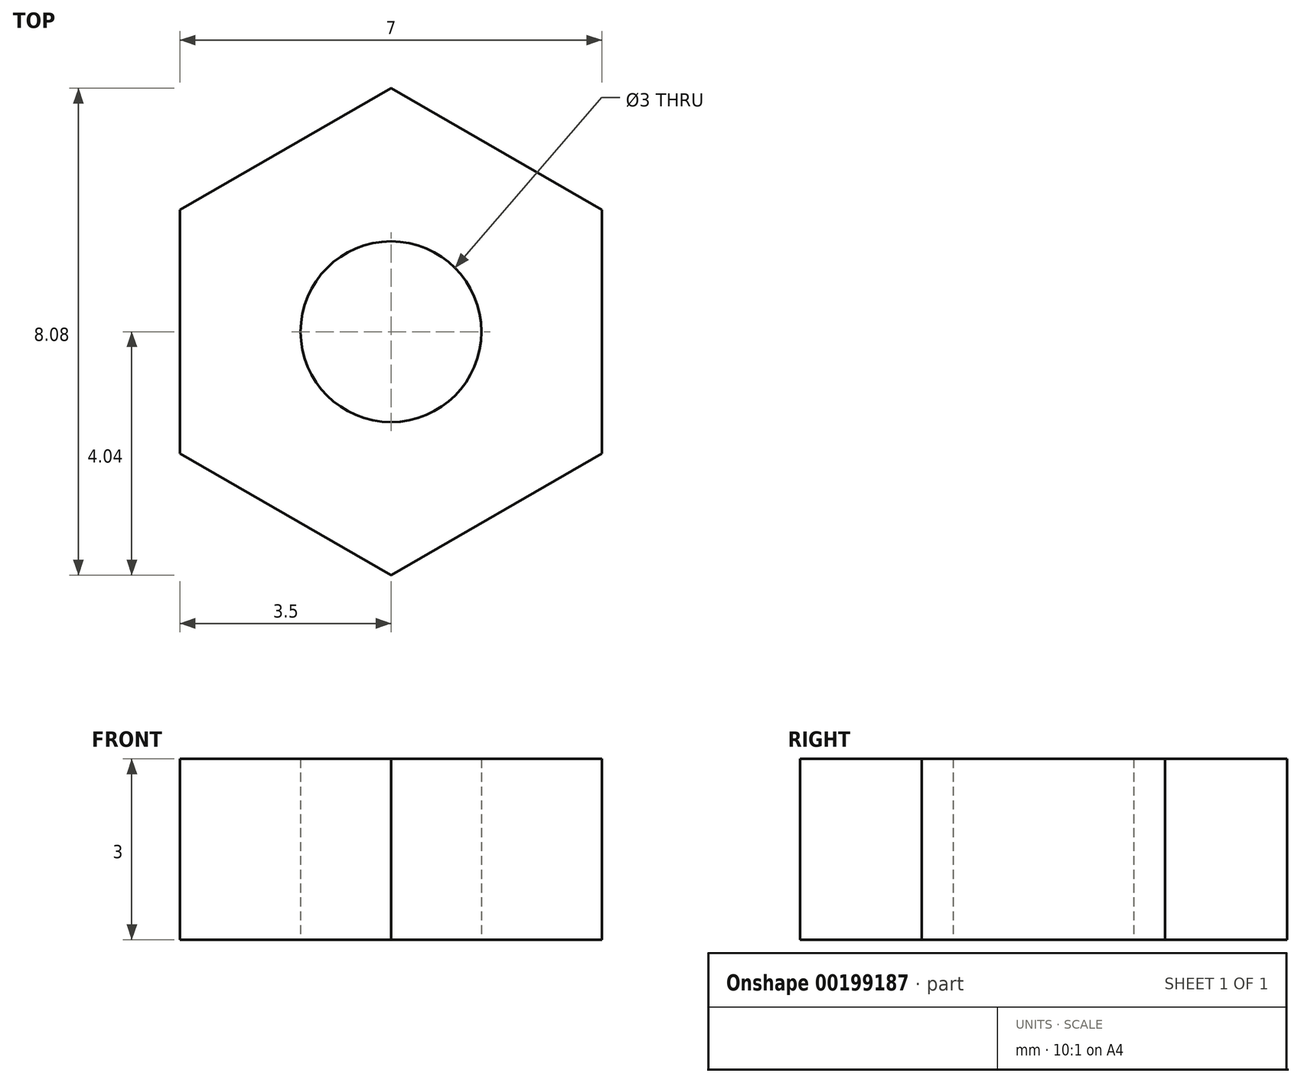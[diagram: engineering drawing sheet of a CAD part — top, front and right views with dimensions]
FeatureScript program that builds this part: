
annotation { "Feature Type Name" : "Feature", "Feature Type Description" : "" }
export const myFeature = defineFeature(function(context is Context, id is Id, definition is map)
    precondition{}
    {
        {
            var Q0;
            Q0=qCreatedBy(makeId("Top.planeOp"),FACE);
            var sketch = newSketch(context, id + "F0", { "sketchPlane" : qUnion([Q0])});
            skCircle(sketch, "E0", {"center": v(0, 0) * mm, "radius": 1.5 * mm});
            skLineSegment(sketch, "E1.0", {"start": v(-3.5, -2.02) * mm, "end": v(-3.5, 2.02) * mm});
            skLineSegment(sketch, "E1.1", {"start": v(-3.5, 2.02) * mm, "end": v(0, 4.04) * mm});
            skLineSegment(sketch, "E1.2", {"start": v(0, 4.04) * mm, "end": v(3.5, 2.02) * mm});
            skLineSegment(sketch, "E1.3", {"start": v(3.5, 2.02) * mm, "end": v(3.5, -2.02) * mm});
            skLineSegment(sketch, "E1.4", {"start": v(3.5, -2.02) * mm, "end": v(0, -4.04) * mm});
            skLineSegment(sketch, "E1.5", {"start": v(0, -4.04) * mm, "end": v(-3.5, -2.02) * mm});
            skPoint(sketch, "E1.0.midPoint", {"position": v(-3.5, 0) * mm});
            skSolve(sketch);
        }
        {
            var Q0;
            Q0 = qSketchRegion(id + "F0", true);
            var Q1;
            Q1=makeQuery(id+"F0.imprint","IMPRINT",FACE,{"disambiguationData":[TD([[makeQuery(id+"F0.imprint","IMPRINT",EDGE,{"derivedFrom":sQuery(id+"F0.wireOp",EDGE,"E0")}),-1.0]])]});
            extrude(context, id + "F1", {"entities" : qUnion([Q0, Q1]), "depth" : 3 * mm});
        }
    });
